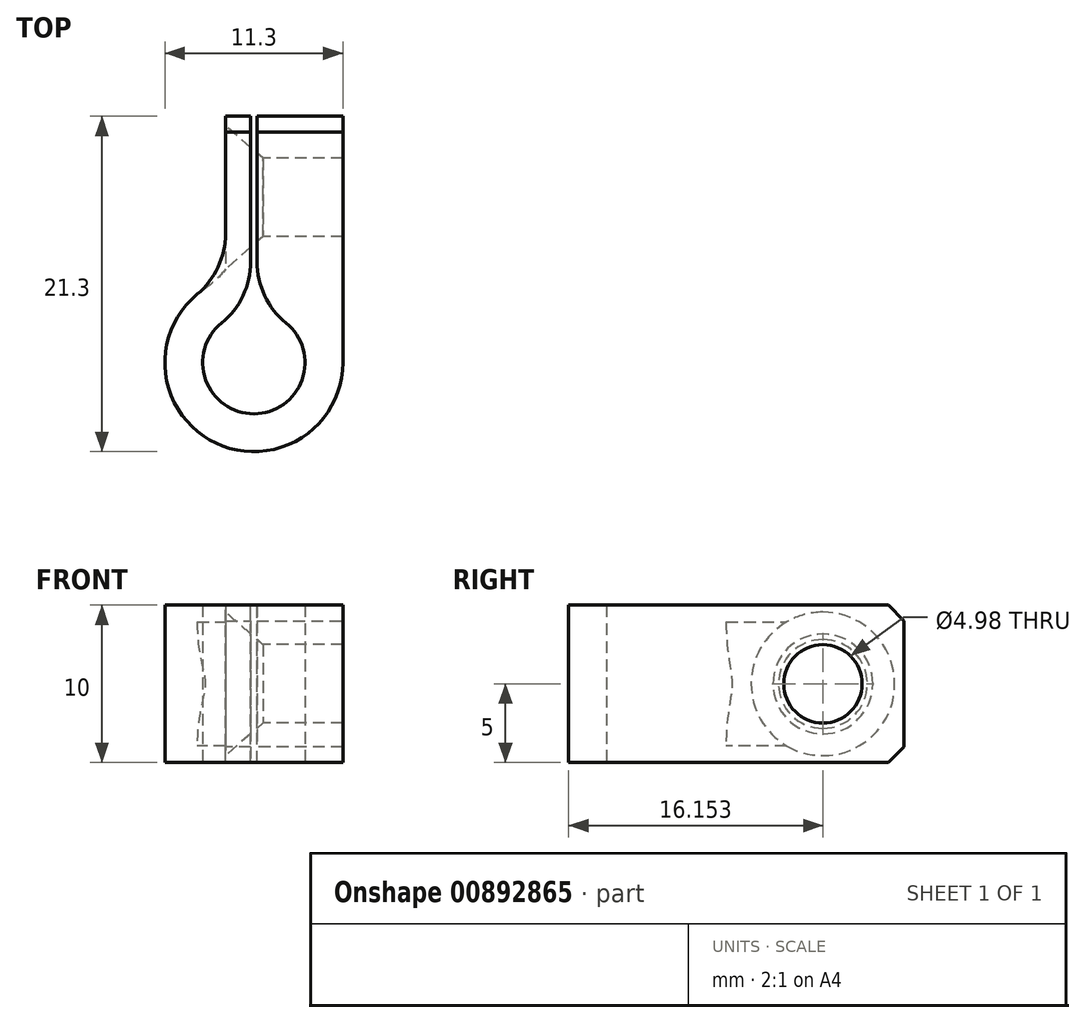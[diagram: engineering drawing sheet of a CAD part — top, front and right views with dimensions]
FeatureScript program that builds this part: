
annotation { "Feature Type Name" : "Feature", "Feature Type Description" : "" }
export const myFeature = defineFeature(function(context is Context, id is Id, definition is map)
    precondition{}
    {
        {
            var Q0;
            Q0=qCreatedBy(makeId("Top.planeOp"),FACE);
            var sketch = newSketch(context, id + "F0", { "sketchPlane" : qUnion([Q0])});
            skCircle(sketch, "E0", {"center": v(0, 0) * mm, "radius": 3.25 * mm});
            skCircle(sketch, "E1", {"center": v(0, 0) * mm, "radius": 5.65 * mm});
            skLineSegment(sketch, "E2", {"start": v(5.65, 0) * mm, "end": v(5.65, 15.65) * mm});
            skLineSegment(sketch, "E3", {"start": v(5.65, 15.65) * mm, "end": v(0.2, 15.65) * mm});
            skLineSegment(sketch, "E4", {"start": v(0.2, 15.65) * mm, "end": v(0.2, 5.65) * mm});
            skLineSegment(sketch, "E5", {"start": v(-0.2, 5.65) * mm, "end": v(-0.2, 15.65) * mm});
            skLineSegment(sketch, "E6", {"start": v(-0.2, 15.65) * mm, "end": v(-1.8, 15.65) * mm});
            skLineSegment(sketch, "E7", {"start": v(-1.8, 15.65) * mm, "end": v(-1.8, 5.36) * mm});
            skLineSegment(sketch, "E8", {"start": v(0, 0) * mm, "end": v(0, 5.65) * mm, "construction": true});
            skLineSegment(sketch, "E9", {"start": v(-0.2, 5.65) * mm, "end": v(-0.2, 3.24) * mm});
            skLineSegment(sketch, "E10", {"start": v(0.2, 5.65) * mm, "end": v(0.2, 3.24) * mm});
            skSolve(sketch);
        }
        {
            var Q0;
            {var subQ0=sQuery(id+"F0.wireOp",EDGE,"E5");Q0=makeQuery(id+"F0.imprint","IMPRINT",FACE,{"disambiguationData":[TD([[makeQuery(id+"F0.imprint","IMPRINT",EDGE,{"derivedFrom":subQ0}),1.0]])]});}
            var Q1;
            {var subQ0=sQuery(id+"F0.wireOp",EDGE,"E2");Q1=makeQuery(id+"F0.imprint","IMPRINT",FACE,{"disambiguationData":[TD([[makeQuery(id+"F0.imprint","IMPRINT",EDGE,{"derivedFrom":subQ0}),1.0]])]});}
            var Q2;
            {var subQ3=sQuery(id+"F0.wireOp",EDGE,"E9");Q2=makeQuery(id+"F0.imprint","IMPRINT",FACE,{"disambiguationData":[TD([[makeQuery(id+"F0.imprint","IMPRINT",EDGE,{"derivedFrom":subQ3}),-1.0]])]});}
            extrude(context, id + "F1", {"entities" : qUnion([Q0, Q1, Q2]), "endBound" : BoundingType.SYMMETRIC, "depth" : 10 * mm, "offsetDistance" : 25 * mm});
        }
        {
            var Q0;
            Q0=makeQuery(id+"F1.opExtrude","SWEPT_FACE",FACE,{"disambiguationData":[OSD([sQuery(id+"F0.wireOp",EDGE,"E7")])]});
            var sketch = newSketch(context, id + "F2", { "sketchPlane" : qUnion([Q0])});
            skLineSegment(sketch, "E11", {"start": v(-15.65, -5) * mm, "end": v(-5.36, 5) * mm, "construction": true});
            skPoint(sketch, "E12", {"position": v(-10.5, 0) * mm});
            skSolve(sketch);
        }
        {
            var Q0;
            Q0=sQuery(id+"F2.wireOp",VERTEX,"E12");
            var Q1;
            Q1=makeQuery(id+"F1.opExtrude","SWEPT_BODY",BODY,{"disambiguationData":[OSD([sQuery(id+"F0.wireOp",EDGE,"E0"),sQuery(id+"F0.wireOp",EDGE,"E1"),sQuery(id+"F0.wireOp",EDGE,"E2"),sQuery(id+"F0.wireOp",EDGE,"E3"),sQuery(id+"F0.wireOp",EDGE,"E4"),sQuery(id+"F0.wireOp",EDGE,"E5"),sQuery(id+"F0.wireOp",EDGE,"E6"),sQuery(id+"F0.wireOp",EDGE,"E7"),sQuery(id+"F0.wireOp",EDGE,"E9"),sQuery(id+"F0.wireOp",EDGE,"E10")])]});
            hole(context, id + "F3", {"style" : HoleStyle.C_SINK, "endStyle" : HoleEndStyle.THROUGH, "standardTappedOrClearance" : lookupTablePath({ "fit" : "Normal (ASME)", "standard" : "ANSI", "size" : "#8", "type" : "Clearance" }), "standardBlindInLast" : lookupTablePath({ "fit" : "Normal", "standard" : "ANSI", "size" : "#8", "type" : "Clearance" }), "holeDiameter" : 4.98 * mm, "cSinkDiameter" : 9.12 * mm, "cSinkAngle" : 82 * degree, "majorDiameter" : 5 * mm, "isTappedThrough" : true, "tappedDepth" : 12 * mm, "tapClearance" : 3, "startFromSketch" : true, "locations" : qUnion([Q0]), "scope" : qUnion([Q1])});
        }
        {
            var Q0;
            Q0=makeQuery(id+"F1.opExtrude","SWEPT_EDGE",EDGE,{"disambiguationData":[OSD([sQuery(id+"F0.wireOp",EDGE,"E1"),sQuery(id+"F0.wireOp",EDGE,"E7")])]});
            fillet(context, id + "F4", {"entities" : qUnion([Q0]), "radius" : 5 * mm, "tangentPropagation" : true, "allowEdgeOverflow" : false});
        }
        {
            var Q0;
            Q0=makeQuery(id+"F1.opExtrude","CAP_EDGE",EDGE,{"disambiguationData":[OSD([sQuery(id+"F0.wireOp",EDGE,"E3")])],"isStart":true});
            var Q1;
            Q1=makeQuery(id+"F1.opExtrude","CAP_EDGE",EDGE,{"disambiguationData":[OSD([sQuery(id+"F0.wireOp",EDGE,"E6")])],"isStart":true});
            var Q2;
            Q2=makeQuery(id+"F1.opExtrude","CAP_EDGE",EDGE,{"disambiguationData":[OSD([sQuery(id+"F0.wireOp",EDGE,"E6")])],"isStart":false});
            var Q3;
            Q3=makeQuery(id+"F1.opExtrude","CAP_EDGE",EDGE,{"disambiguationData":[OSD([sQuery(id+"F0.wireOp",EDGE,"E3")])],"isStart":false});
            chamfer(context, id + "F5", {"entities" : qUnion([Q0, Q1, Q2, Q3]), "width" : 1 * mm, "tangentPropagation" : true});
        }
        {
            var Q0;
            Q0=makeQuery(id+"F1.opExtrude","SWEPT_EDGE",EDGE,{"disambiguationData":[OSD([sQuery(id+"F0.wireOp",EDGE,"E0"),sQuery(id+"F0.wireOp",EDGE,"E10")])]});
            var Q1;
            Q1=makeQuery(id+"F1.opExtrude","SWEPT_EDGE",EDGE,{"disambiguationData":[OSD([sQuery(id+"F0.wireOp",EDGE,"E0"),sQuery(id+"F0.wireOp",EDGE,"E9")])]});
            fillet(context, id + "F6", {"entities" : qUnion([Q0, Q1]), "radius" : 5 * mm, "tangentPropagation" : true, "allowEdgeOverflow" : false});
        }
    });
